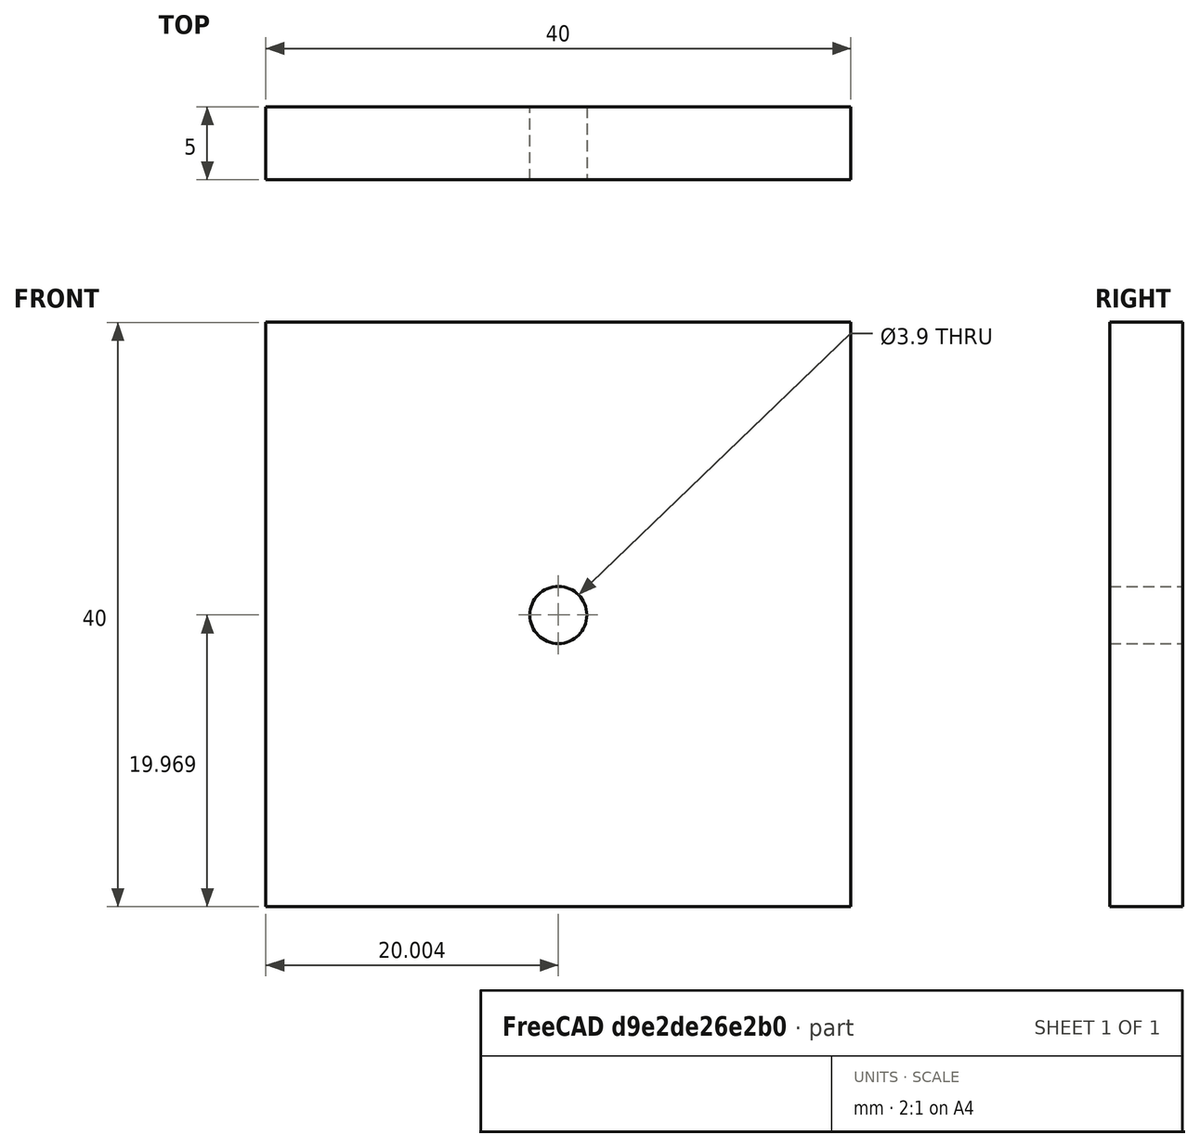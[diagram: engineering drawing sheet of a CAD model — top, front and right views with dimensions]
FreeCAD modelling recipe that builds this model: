
FCSTD DOCUMENT  (FreeCAD 0.17R13541 (Git))
Label: 40x40x5squarewithholeinmid
License: All rights reserved
LicenseURL: http://en.wikipedia.org/wiki/All_rights_reserved
objects: Sketcher::SketchObject×1, Part::Extrusion×1
note: 2 computed .brp shape members not serialized (recipe doc carries the construction recipe); baked Part::Feature solids carry a one-line shape summary decoded from their .brp

FEATURE [Sketcher::SketchObject] Sketch
  Placement = pos=(0,0,0) rot=(-1,0,0;4.71239rad)
  sketch-geometry (5):
    g0: LineSegment StartX=-11.0656 StartY=15.173 StartZ=0 EndX=28.9344 EndY=15.173 EndZ=0
    g1: LineSegment StartX=28.9344 StartY=15.173 StartZ=0 EndX=28.9344 EndY=-24.827 EndZ=0
    g2: LineSegment StartX=28.9344 StartY=-24.827 StartZ=0 EndX=-11.0656 EndY=-24.827 EndZ=0
    g3: LineSegment StartX=-11.0656 StartY=-24.827 StartZ=0 EndX=-11.0656 EndY=15.173 EndZ=0
    g4: Circle CenterX=8.93435 CenterY=-4.86053 CenterZ=0 NormalX=0 NormalY=0 NormalZ=1 AngleXU=0 Radius=1.95
  constraints (13):
    c: Coincident(g0,g1)
    c: Coincident(g1,g2)
    c: Coincident(g2,g3)
    c: Coincident(g3,g0)
    c: Horizontal(g0)
    c: Horizontal(g2)
    c: Vertical(g1)
    c: Vertical(g3)
    c: Equal(g0,g1)
    c: Equal(g1,g2)
    c: Equal(g2,g3)
    c: Distance(g0) = 40
    c: Radius(g4) = 1.95
FEATURE [Part::Extrusion] Extrude
  Base = -> Sketch
  Dir = (0,-1,0)
  DirMode = 2
  FaceMakerClass = Part::FaceMakerBullseye
  LengthFwd = 5
  LengthRev = 0
  Solid = true
  Symmetric = false
